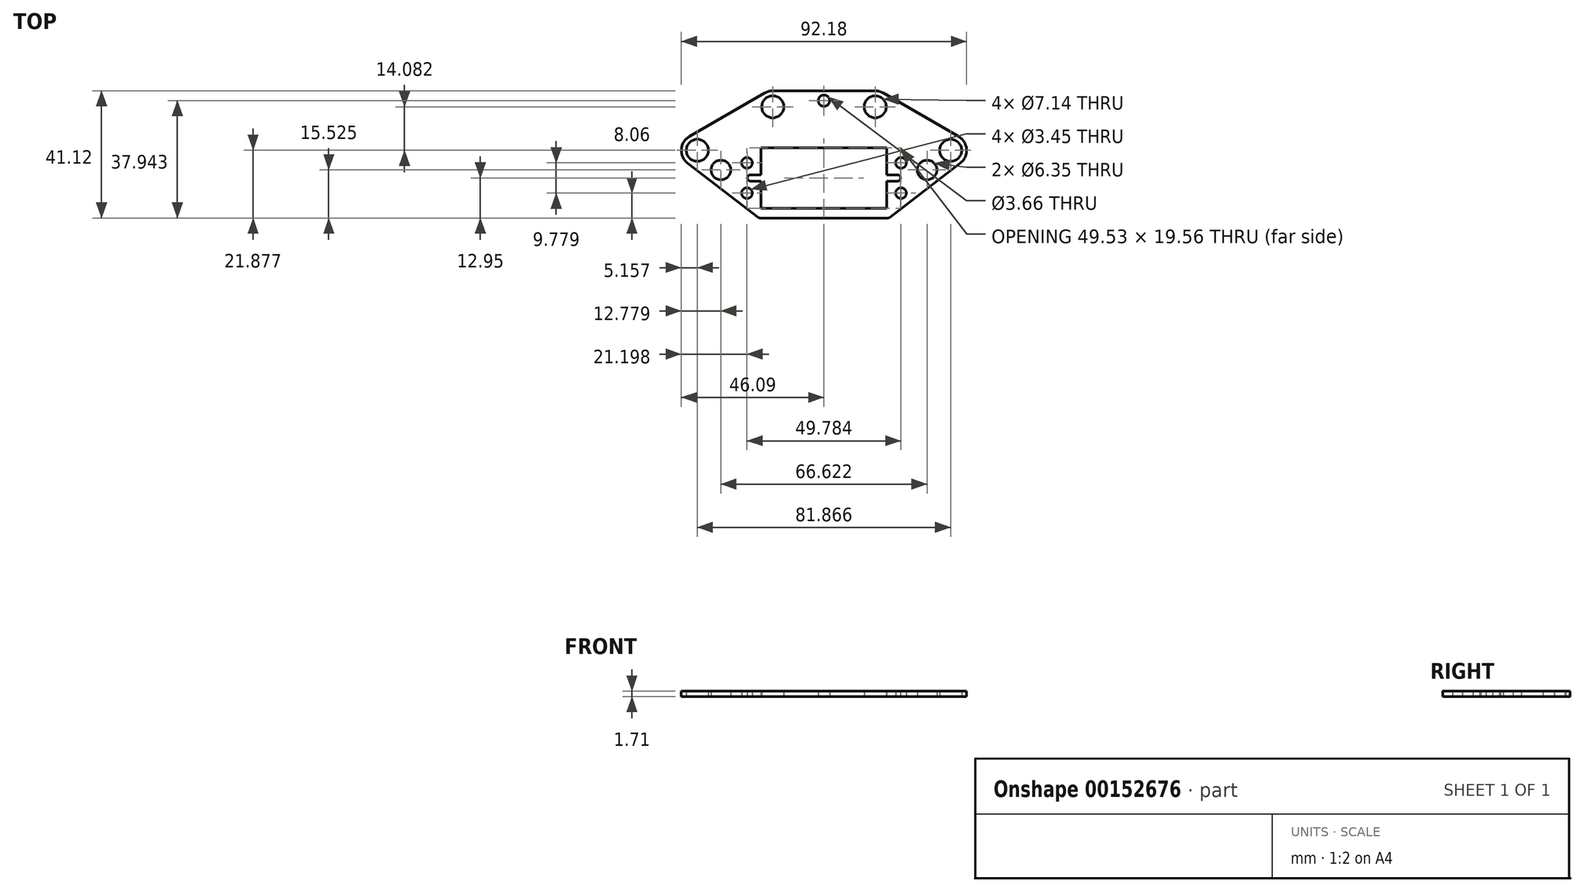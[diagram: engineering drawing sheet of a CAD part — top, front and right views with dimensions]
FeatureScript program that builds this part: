
annotation { "Feature Type Name" : "Feature", "Feature Type Description" : "" }
export const myFeature = defineFeature(function(context is Context, id is Id, definition is map)
    precondition{}
    {
        {
            var Q0;
            Q0=qCreatedBy(makeId("Top.planeOp"),FACE);
            var sketch = newSketch(context, id + "F0", { "sketchPlane" : qUnion([Q0])});
            skLineSegment(sketch, "E0.bottom", {"start": v(20.32, -1.02) * mm, "end": v(23.75, -1.02) * mm});
            skLineSegment(sketch, "E0.top", {"start": v(20.32, 1.02) * mm, "end": v(23.75, 1.02) * mm});
            skLineSegment(sketch, "E0.left", {"start": v(20.32, -1.02) * mm, "end": v(20.32, 1.02) * mm, "construction": true});
            skLineSegment(sketch, "E0.right", {"start": v(23.75, -1.02) * mm, "end": v(23.75, 1.02) * mm, "construction": true});
            skLineSegment(sketch, "E1.top", {"start": v(20.32, -9.78) * mm, "end": v(-20.32, -9.78) * mm});
            skLineSegment(sketch, "E1.left", {"start": v(20.32, -1.02) * mm, "end": v(20.32, -9.78) * mm});
            skLineSegment(sketch, "E1.right", {"start": v(-20.32, -1.02) * mm, "end": v(-20.32, -9.78) * mm});
            skLineSegment(sketch, "E2.bottom", {"start": v(-20.32, -1.02) * mm, "end": v(-23.75, -1.02) * mm});
            skLineSegment(sketch, "E2.top", {"start": v(-20.32, 1.02) * mm, "end": v(-23.75, 1.02) * mm});
            skLineSegment(sketch, "E2.left", {"start": v(-20.32, -1.02) * mm, "end": v(-20.32, 1.02) * mm, "construction": true});
            skLineSegment(sketch, "E2.right", {"start": v(-23.75, -1.02) * mm, "end": v(-23.75, 1.02) * mm, "construction": true});
            skLineSegment(sketch, "E3.top", {"start": v(20.32, 9.78) * mm, "end": v(-20.32, 9.78) * mm});
            skLineSegment(sketch, "E3.left", {"start": v(20.32, 1.02) * mm, "end": v(20.32, 9.78) * mm});
            skLineSegment(sketch, "E3.right", {"start": v(-20.32, 1.02) * mm, "end": v(-20.32, 9.78) * mm});
            skArc(sketch, "E4", {"start": v(23.75, -1.02) * mm, "mid": v(24.77, 0) * mm, "end": v(23.75, 1.02) * mm});
            skArc(sketch, "E5", {"start": v(-23.75, 1.02) * mm, "mid": v(-24.76, 0) * mm, "end": v(-23.75, -1.02) * mm});
            skLineSegment(sketch, "E6", {"start": v(0, -9.78) * mm, "end": v(0, 9.78) * mm, "construction": true});
            skLineSegment(sketch, "E7.bottom", {"start": v(24.9, 4.89) * mm, "end": v(-24.9, 4.89) * mm, "construction": true});
            skLineSegment(sketch, "E7.top", {"start": v(24.9, -4.89) * mm, "end": v(-24.9, -4.89) * mm, "construction": true});
            skLineSegment(sketch, "E7.left", {"start": v(24.9, 4.89) * mm, "end": v(24.9, -4.89) * mm, "construction": true});
            skLineSegment(sketch, "E7.right", {"start": v(-24.9, 4.89) * mm, "end": v(-24.9, -4.89) * mm, "construction": true});
            skPoint(sketch, "E7.middle", {"position": v(0, 0) * mm});
            skCircle(sketch, "E8", {"center": v(-24.9, 4.89) * mm, "radius": 1.73 * mm});
            skCircle(sketch, "E9", {"center": v(-24.9, -4.89) * mm, "radius": 1.73 * mm});
            skCircle(sketch, "E10", {"center": v(24.9, -4.89) * mm, "radius": 1.73 * mm});
            skCircle(sketch, "E11", {"center": v(24.9, 4.89) * mm, "radius": 1.73 * mm});
            skLineSegment(sketch, "E12", {"start": v(-20.32, 0) * mm, "end": v(-10.9, 0) * mm, "construction": true});
            skLineSegment(sketch, "E13", {"start": v(0, 9.78) * mm, "end": v(0, 23) * mm, "construction": true});
            skLineSegment(sketch, "E14", {"start": v(-16.54, 23) * mm, "end": v(16.54, 23) * mm, "construction": true});
            skLineSegment(sketch, "E15", {"start": v(16.54, 23) * mm, "end": v(40.93, 8.93) * mm, "construction": true});
            skLineSegment(sketch, "E16", {"start": v(-16.54, 23) * mm, "end": v(-40.93, 8.93) * mm, "construction": true});
            skCircle(sketch, "E17", {"center": v(40.93, 8.93) * mm, "radius": 3.57 * mm});
            skCircle(sketch, "E18", {"center": v(16.54, 23) * mm, "radius": 3.57 * mm});
            skCircle(sketch, "E19", {"center": v(-16.54, 23) * mm, "radius": 3.57 * mm});
            skCircle(sketch, "E20", {"center": v(-40.93, 8.93) * mm, "radius": 3.57 * mm});
            skLineSegment(sketch, "E21", {"start": v(-16.54, 23) * mm, "end": v(-10.9, 0) * mm, "construction": true});
            skLineSegment(sketch, "E22", {"start": v(0, 23) * mm, "end": v(0, 28.17) * mm, "construction": true});
            skLineSegment(sketch, "E23", {"start": v(40.93, 8.93) * mm, "end": v(0, 8.93) * mm, "construction": true});
            skLineSegment(sketch, "E24", {"start": v(0, 8.93) * mm, "end": v(-40.93, 8.93) * mm, "construction": true});
            skLineSegment(sketch, "E25", {"start": v(-16.54, 28.17) * mm, "end": v(16.54, 28.17) * mm});
            skArc(sketch, "E26", {"start": v(44.07, 4.83) * mm, "mid": v(46.08, 9.26) * mm, "end": v(43.51, 13.4) * mm});
            skArc(sketch, "E27", {"start": v(19.12, 27.48) * mm, "mid": v(17.88, 28) * mm, "end": v(16.54, 28.17) * mm});
            skArc(sketch, "E28", {"start": v(-16.54, 28.17) * mm, "mid": v(-17.88, 28) * mm, "end": v(-19.12, 27.48) * mm});
            skArc(sketch, "E29", {"start": v(-43.51, 13.4) * mm, "mid": v(-46.08, 9.26) * mm, "end": v(-44.07, 4.83) * mm});
            skLineSegment(sketch, "E30", {"start": v(19.12, 27.48) * mm, "end": v(43.51, 13.4) * mm});
            skLineSegment(sketch, "E31", {"start": v(-19.12, 27.48) * mm, "end": v(-43.51, 13.4) * mm});
            skLineSegment(sketch, "E32", {"start": v(-44.07, 4.83) * mm, "end": v(-21.11, -12.8) * mm});
            skLineSegment(sketch, "E33", {"start": v(44.07, 4.83) * mm, "end": v(21.11, -12.8) * mm});
            skArc(sketch, "E34", {"start": v(20.65, -12.95) * mm, "mid": v(20.9, -12.91) * mm, "end": v(21.11, -12.8) * mm});
            skLineSegment(sketch, "E35", {"start": v(-20.65, -12.95) * mm, "end": v(20.65, -12.95) * mm});
            skCircle(sketch, "E36", {"center": v(24.9, -4.89) * mm, "radius": 3.97 * mm, "construction": true});
            skLineSegment(sketch, "E37", {"start": v(24.9, -4.89) * mm, "end": v(33.31, 2.57) * mm, "construction": true});
            skCircle(sketch, "E38", {"center": v(33.31, 2.57) * mm, "radius": 4.76 * mm, "construction": true});
            skCircle(sketch, "E39", {"center": v(33.31, 2.57) * mm, "radius": 3.18 * mm});
            skLineSegment(sketch, "E40", {"start": v(-24.9, -4.89) * mm, "end": v(-33.31, 2.57) * mm, "construction": true});
            skCircle(sketch, "E41", {"center": v(-33.31, 2.57) * mm, "radius": 4.76 * mm, "construction": true});
            skCircle(sketch, "E42", {"center": v(-33.31, 2.57) * mm, "radius": 3.18 * mm});
            skCircle(sketch, "E43", {"center": v(24.9, 4.89) * mm, "radius": 3.97 * mm, "construction": true});
            skArc(sketch, "E44", {"start": v(43.51, 13.4) * mm, "mid": v(35.78, 8.59) * mm, "end": v(44.07, 4.83) * mm, "construction": true});
            skCircle(sketch, "E45", {"center": v(0, 25) * mm, "radius": 1.83 * mm});
            skLineSegment(sketch, "E46", {"start": v(0, -9.78) * mm, "end": v(0, -12.95) * mm, "construction": true});
            skArc(sketch, "E47", {"start": v(-21.11, -12.8) * mm, "mid": v(-20.9, -12.91) * mm, "end": v(-20.65, -12.95) * mm});
            skSolve(sketch);
        }
        {
            var Q0;
            Q0=qSketchRegion(id+"F0",true);
            extrude(context, id + "F1", {"entities" : qUnion([Q0]), "depth" : 1.7 * mm});
        }
    });
